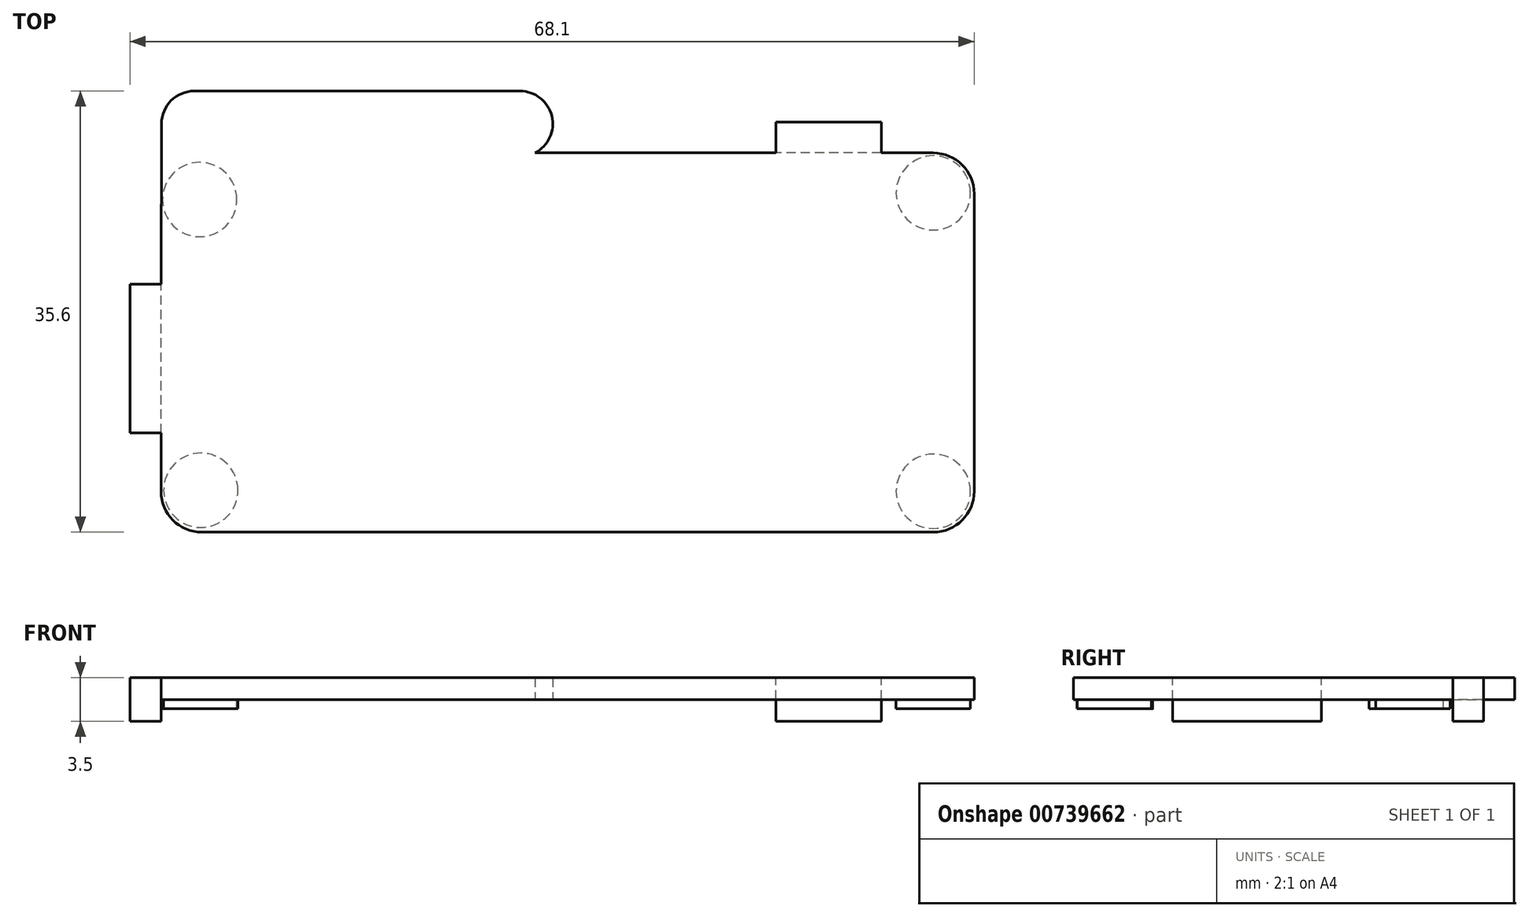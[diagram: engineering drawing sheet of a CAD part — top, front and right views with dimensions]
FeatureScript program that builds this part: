
annotation { "Feature Type Name" : "Feature", "Feature Type Description" : "" }
export const myFeature = defineFeature(function(context is Context, id is Id, definition is map)
    precondition{}
    {
        {
            var Q0;
            Q0=qCreatedBy(makeId("Top.planeOp"),FACE);
            var sketch = newSketch(context, id + "F0", { "sketchPlane" : qUnion([Q0])});
            skArc(sketch, "E0.0", {"start": v(-29.3, -16.64) * mm, "mid": v(-28.33, -18.97) * mm, "end": v(-26, -19.94) * mm});
            skLineSegment(sketch, "E0.1", {"start": v(-29.3, -0.11) * mm, "end": v(-29.3, -16.64) * mm});
            skLineSegment(sketch, "E0.2", {"start": v(-29.26, 13.02) * mm, "end": v(-29.3, -0.11) * mm});
            skArc(sketch, "E0.3", {"start": v(-26.61, 15.66) * mm, "mid": v(-28.48, 14.9) * mm, "end": v(-29.26, 13.02) * mm});
            skLineSegment(sketch, "E0.4", {"start": v(-0.35, 15.66) * mm, "end": v(-26.61, 15.66) * mm});
            skLineSegment(sketch, "E0.5", {"start": v(-26, -19.94) * mm, "end": v(33, -19.94) * mm});
            skArc(sketch, "E0.6", {"start": v(33, -19.94) * mm, "mid": v(35.33, -18.97) * mm, "end": v(36.3, -16.64) * mm});
            skLineSegment(sketch, "E0.7", {"start": v(36.3, -16.64) * mm, "end": v(36.3, 7.36) * mm});
            skArc(sketch, "E0.8", {"start": v(36.3, 7.36) * mm, "mid": v(35.33, 9.7) * mm, "end": v(33, 10.66) * mm});
            skLineSegment(sketch, "E0.9", {"start": v(33, 10.66) * mm, "end": v(0.87, 10.66) * mm});
            skArc(sketch, "E0.10", {"start": v(0.87, 10.66) * mm, "mid": v(2.22, 13.64) * mm, "end": v(-0.35, 15.66) * mm});
            skSolve(sketch);
        }
        {
            var Q0;
            Q0=makeQuery(id+"F0.imprint","IMPRINT",FACE,{"disambiguationData":[TD([[makeQuery(id+"F0.imprint","IMPRINT",EDGE,{"derivedFrom":sQuery(id+"F0.wireOp",EDGE,"E0.0")}),1.0]])]});
            extrude(context, id + "F1", {"entities" : qUnion([Q0]), "depth" : 1.75 * mm, "offsetDistance" : 25 * mm});
        }
        {
            var Q0;
            Q0=makeQuery(id+"F1.opExtrude","CAP_FACE",FACE,{"disambiguationData":[OSD([sQuery(id+"F0.wireOp",EDGE,"E0.0"),sQuery(id+"F0.wireOp",EDGE,"E0.1"),sQuery(id+"F0.wireOp",EDGE,"E0.2"),sQuery(id+"F0.wireOp",EDGE,"E0.3"),sQuery(id+"F0.wireOp",EDGE,"E0.4"),sQuery(id+"F0.wireOp",EDGE,"E0.5"),sQuery(id+"F0.wireOp",EDGE,"E0.6"),sQuery(id+"F0.wireOp",EDGE,"E0.7"),sQuery(id+"F0.wireOp",EDGE,"E0.8"),sQuery(id+"F0.wireOp",EDGE,"E0.9"),sQuery(id+"F0.wireOp",EDGE,"E0.10")])],"isStart":true});
            var sketch = newSketch(context, id + "F2", { "sketchPlane" : qUnion([Q0])});
            skLineSegment(sketch, "E1.bottom", {"start": v(28.8, -10.66) * mm, "end": v(20.3, -10.66) * mm});
            skLineSegment(sketch, "E1.top", {"start": v(28.8, -13.16) * mm, "end": v(20.3, -13.16) * mm});
            skLineSegment(sketch, "E1.left", {"start": v(28.8, -10.66) * mm, "end": v(28.8, -13.16) * mm});
            skLineSegment(sketch, "E1.right", {"start": v(20.3, -10.66) * mm, "end": v(20.3, -13.16) * mm});
            skLineSegment(sketch, "E2.bottom", {"start": v(-29.3, -0.06) * mm, "end": v(-31.8, -0.06) * mm});
            skLineSegment(sketch, "E2.top", {"start": v(-29.3, 11.94) * mm, "end": v(-31.8, 11.94) * mm});
            skLineSegment(sketch, "E2.left", {"start": v(-29.3, -0.06) * mm, "end": v(-29.3, 11.94) * mm});
            skLineSegment(sketch, "E2.right", {"start": v(-31.8, -0.06) * mm, "end": v(-31.8, 11.94) * mm});
            skSolve(sketch);
        }
        {
            var Q0;
            Q0 = qSketchRegion(id + "F2", true);
            extrude(context, id + "F3", {"entities" : qUnion([Q0]), "operationType" : NewBodyOperationType.ADD, "endBound" : BoundingType.SYMMETRIC, "depth" : 3.5 * mm, "offsetDistance" : 25 * mm});
        }
        {
            var Q0;
            Q0=makeQuery(id+"F0.imprint","IMPRINT",FACE,{"disambiguationData":[TD([[makeQuery(id+"F0.imprint","IMPRINT",EDGE,{"derivedFrom":sQuery(id+"F0.wireOp",EDGE,"E0.0")}),1.0]])]});
            var sketch = newSketch(context, id + "F4", { "sketchPlane" : qUnion([Q0])});
            skCircle(sketch, "E3", {"center": v(33, -16.64) * mm, "radius": 3 * mm});
            skCircle(sketch, "E4", {"center": v(33, 7.44) * mm, "radius": 3 * mm});
            skCircle(sketch, "E5", {"center": v(-26.1, -16.55) * mm, "radius": 3 * mm});
            skCircle(sketch, "E6", {"center": v(-26.18, 6.9) * mm, "radius": 3 * mm});
            skSolve(sketch);
        }
        {
            var Q0;
            Q0 = qSketchRegion(id + "F4", true);
            extrude(context, id + "F5", {"entities" : qUnion([Q0]), "operationType" : NewBodyOperationType.ADD, "oppositeDirection" : true, "depth" : .75 * mm, "offsetDistance" : 25 * mm});
        }
    });
